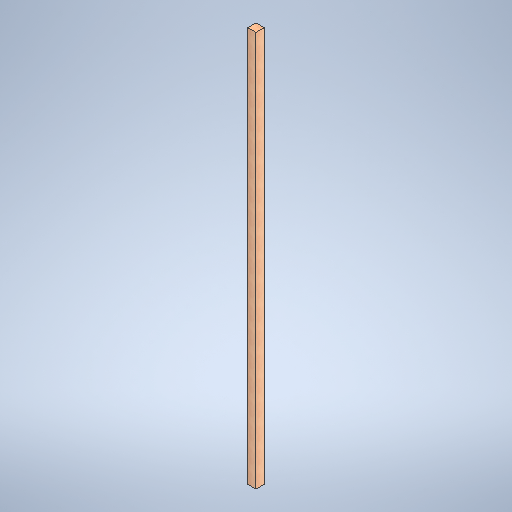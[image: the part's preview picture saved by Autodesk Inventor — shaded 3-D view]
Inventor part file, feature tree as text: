
AUTODESK INVENTOR PART (.ipt)
format: ipt  version: 2025 (Build 290162000, 162)  size: 306,688 bytes
history: native  units: in
note: dims shown in document units (in); Inventor stores cm internally (conversion verified against a paired STEP export)
features: extrude x1, sketch x1
ambient origin geometry x8: Origin, YZ Plane, XZ Plane, XY Plane, X Axis, Y Axis, Z Axis, Center Point
bodies: Solid1 (feature_tree)
feature tree (2):
  extrude  "Extrusion1"  Depth=4.0in
  sketch  "Sketch1"  dims[d0=4.0in d1=4.0in d2=192.0in d3=0.0in d4=0.5in d5=0.0344in d6=0.5in d7=0.0344in]
